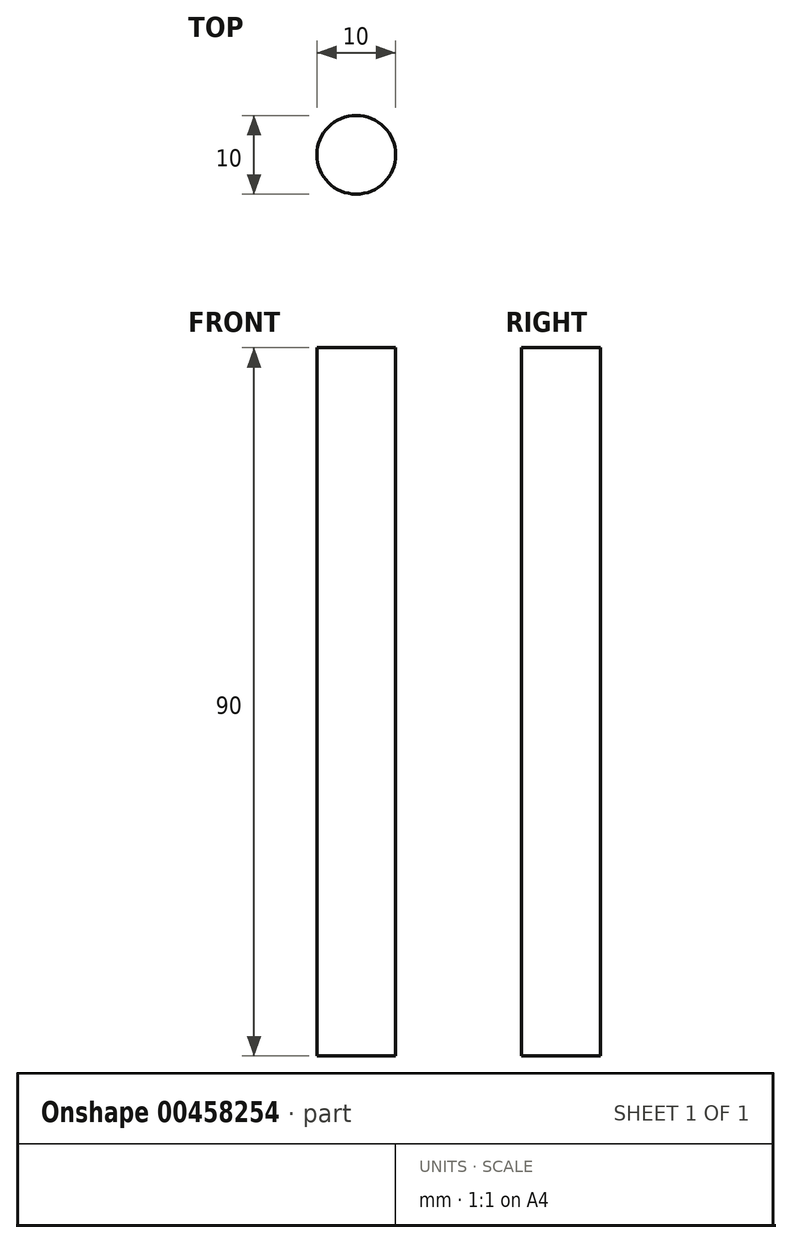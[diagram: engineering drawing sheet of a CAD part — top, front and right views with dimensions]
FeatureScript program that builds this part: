
annotation { "Feature Type Name" : "Feature", "Feature Type Description" : "" }
export const myFeature = defineFeature(function(context is Context, id is Id, definition is map)
    precondition{}
    {
        {
            var Q0;
            Q0=qCreatedBy(makeId("Top.planeOp"),FACE);
            var sketch = newSketch(context, id + "F0", { "sketchPlane" : qUnion([Q0])});
            skCircle(sketch, "E0", {"center": v(0, 0) * mm, "radius": 5 * mm});
            skSolve(sketch);
        }
        {
            var Q0;
            Q0 = qSketchRegion(id + "F0", true);
            extrude(context, id + "F1", {"entities" : qUnion([Q0]), "depth" : 90 * mm});
        }
    });
